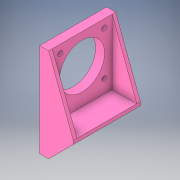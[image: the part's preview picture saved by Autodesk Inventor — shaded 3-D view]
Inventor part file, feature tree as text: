
AUTODESK INVENTOR PART (.ipt)
format: ipt  version: 2019 (Build 230136000, 136)  size: 190,976 bytes
history: native  units: in
note: dims shown in document units (in); Inventor stores cm internally (conversion verified against a paired STEP export)
features: extrude x3, sketch x3, projected_geometry x2
ambient origin geometry x8: Origin, YZ Plane, XZ Plane, XY Plane, X Axis, Y Axis, Z Axis, Center Point
bodies: Body1 (feature_tree)
feature tree (8):
  extrude  "Extrusion2"  Depth=0.1378in
  extrude  "Extrusion3"  Depth=1.6654in
  extrude  "Extrusion5"  Depth=0.1in
  sketch  "Sketch2"  dims[d19=1.2205in d20=0.1378in]
  sketch  "Sketch3"  dims[d21=1.6654in d24=0.2165in]
  sketch  "Sketch5"  dims[d25=0.25in d26=0.0in d27=0.1in d28=0.1in d29=0.1in d30=0.7874in d31=0.6874in d32=0.0in d35=1.25in d36=0.9327in d38=0.7874in d39=1.6654in d40=0.15in d41=0.3937in d42=0.1in d43=1.6654in d44=0.6874in d45=0.0in]
  projected_geometry  "Projected Loop3"
  projected_geometry  "Projected Loop4"
